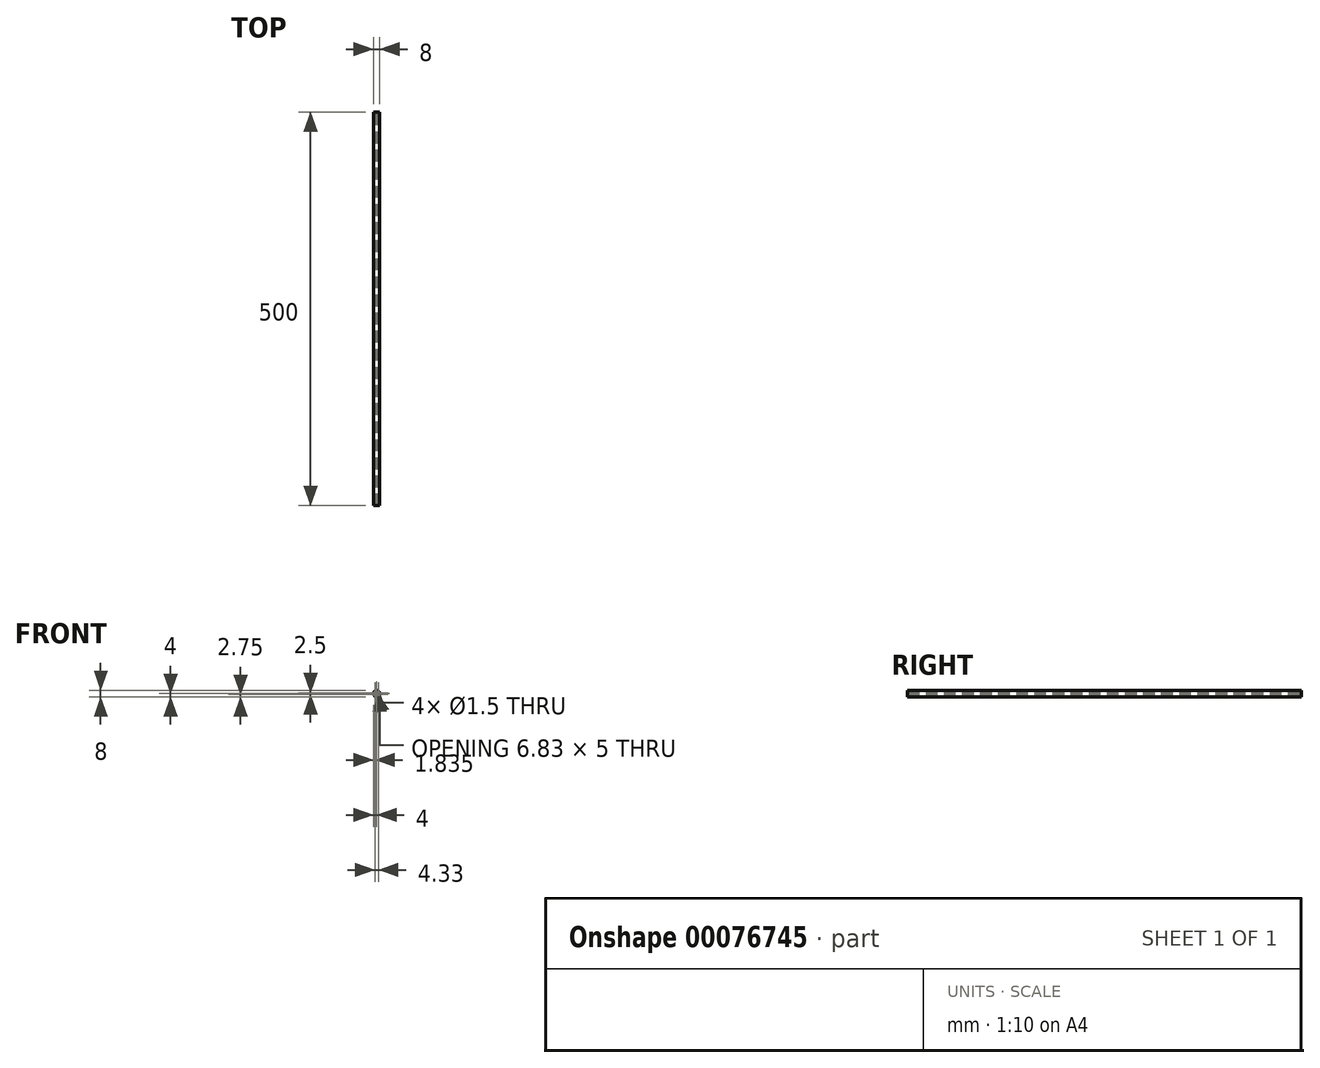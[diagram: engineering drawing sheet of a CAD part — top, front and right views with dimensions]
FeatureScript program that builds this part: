
annotation { "Feature Type Name" : "Feature", "Feature Type Description" : "" }
export const myFeature = defineFeature(function(context is Context, id is Id, definition is map)
    precondition{}
    {
        {
            var Q0;
            Q0=qCreatedBy(makeId("Front.planeOp"),FACE);
            var sketch = newSketch(context, id + "F0", { "sketchPlane" : qUnion([Q0])});
            skCircle(sketch, "E0", {"center": v(0, 1.25) * mm, "radius": 1.25 * mm});
            skCircle(sketch, "E1", {"center": v(0, 1.25) * mm, "radius": 0.75 * mm});
            skCircle(sketch, "E2.MirrorC", {"center": v(0, -1.25) * mm, "radius": 1.25 * mm});
            skCircle(sketch, "E3.MirrorC", {"center": v(0, -1.25) * mm, "radius": 0.75 * mm});
            skCircle(sketch, "E4", {"center": v(2.17, 0) * mm, "radius": 1.25 * mm});
            skCircle(sketch, "E5", {"center": v(2.17, 0) * mm, "radius": 0.75 * mm});
            skCircle(sketch, "E6.MirrorC", {"center": v(-2.17, 0) * mm, "radius": 1.25 * mm});
            skCircle(sketch, "E7.MirrorC", {"center": v(-2.17, 0) * mm, "radius": 0.75 * mm});
            skCircle(sketch, "E8", {"center": v(0, 0) * mm, "radius": 4 * mm});
            skSolve(sketch);
        }
        {
            var Q0;
            Q0=makeQuery(id+"F0.imprint","IMPRINT",FACE,{"disambiguationData":[TD([[makeQuery(id+"F0.imprint","IMPRINT",EDGE,{"derivedFrom":sQuery(id+"F0.wireOp",EDGE,"E8")}),1.0]])]});
            var Q1;
            {var subQ0=sQuery(id+"F0.wireOp",EDGE,"E2.MirrorC");var subQ1=sQuery(id+"F0.wireOp",EDGE,"E0");var subQ2=makeQuery(id+"F0.imprint","INTERSECT",VERTEX,{"derivedFrom":[subQ1,subQ0]});Q1=makeQuery(id+"F0.imprint","IMPRINT",FACE,{"disambiguationData":[TD([[makeQuery(id+"F0.imprint","IMPRINT",EDGE,{"disambiguationData":[TD([[subQ2,-1.0]])],"derivedFrom":subQ1}),-1.0]])]});}
            var Q2;
            {var subQ0=sQuery(id+"F0.wireOp",EDGE,"E2.MirrorC");var subQ1=sQuery(id+"F0.wireOp",EDGE,"E0");var subQ2=makeQuery(id+"F0.imprint","INTERSECT",VERTEX,{"derivedFrom":[subQ1,subQ0]});Q2=makeQuery(id+"F0.imprint","IMPRINT",FACE,{"disambiguationData":[TD([[makeQuery(id+"F0.imprint","IMPRINT",EDGE,{"disambiguationData":[TD([[subQ2,1.0]])],"derivedFrom":subQ1}),-1.0]])]});}
            extrude(context, id + "F1", {"entities" : qUnion([Q0, Q1, Q2]), "endBound" : BoundingType.SYMMETRIC, "depth" : 500 * mm});
        }
        {
            var Q0;
            Q0=makeQuery(id+"F0.imprint","IMPRINT",FACE,{"disambiguationData":[TD([[makeQuery(id+"F0.imprint","IMPRINT",EDGE,{"derivedFrom":sQuery(id+"F0.wireOp",EDGE,"E7.MirrorC")}),1.0]])]});
            var Q1;
            Q1=makeQuery(id+"F0.imprint","IMPRINT",FACE,{"disambiguationData":[TD([[makeQuery(id+"F0.imprint","IMPRINT",EDGE,{"derivedFrom":sQuery(id+"F0.wireOp",EDGE,"E1")}),-1.0]])]});
            var Q2;
            Q2=makeQuery(id+"F0.imprint","IMPRINT",FACE,{"disambiguationData":[TD([[makeQuery(id+"F0.imprint","IMPRINT",EDGE,{"derivedFrom":sQuery(id+"F0.wireOp",EDGE,"E5")}),-1.0]])]});
            var Q3;
            Q3=makeQuery(id+"F0.imprint","IMPRINT",FACE,{"disambiguationData":[TD([[makeQuery(id+"F0.imprint","IMPRINT",EDGE,{"derivedFrom":sQuery(id+"F0.wireOp",EDGE,"E3.MirrorC")}),1.0]])]});
            extrude(context, id + "F2", {"entities" : qUnion([Q0, Q1, Q2, Q3]), "endBound" : BoundingType.SYMMETRIC, "depth" : 500 * mm});
        }
        {
            var Q0;
            Q0=makeQuery(id+"F0.imprint","IMPRINT",FACE,{"disambiguationData":[TD([[makeQuery(id+"F0.imprint","IMPRINT",EDGE,{"derivedFrom":sQuery(id+"F0.wireOp",EDGE,"E7.MirrorC")}),-1.0]])]});
            var Q1;
            Q1=makeQuery(id+"F0.imprint","IMPRINT",FACE,{"disambiguationData":[TD([[makeQuery(id+"F0.imprint","IMPRINT",EDGE,{"derivedFrom":sQuery(id+"F0.wireOp",EDGE,"E3.MirrorC")}),-1.0]])]});
            var Q2;
            Q2=makeQuery(id+"F0.imprint","IMPRINT",FACE,{"disambiguationData":[TD([[makeQuery(id+"F0.imprint","IMPRINT",EDGE,{"derivedFrom":sQuery(id+"F0.wireOp",EDGE,"E5")}),1.0]])]});
            var Q3;
            Q3=makeQuery(id+"F0.imprint","IMPRINT",FACE,{"disambiguationData":[TD([[makeQuery(id+"F0.imprint","IMPRINT",EDGE,{"derivedFrom":sQuery(id+"F0.wireOp",EDGE,"E1")}),1.0]])]});
            extrude(context, id + "F3", {"entities" : qUnion([Q0, Q1, Q2, Q3]), "endBound" : BoundingType.SYMMETRIC, "depth" : 500 * mm});
        }
    });
